# Revit family: Toilet_Universal-Wall_Hung-Sloan-ST-2469_Series
name_source: partatom
category: Plumbing Fixtures
revit_build: Autodesk Revit 2014 (Build: 20130308_1515(x64)
units: mm (PartAtom-declared; Revit-internal decimal feet)

## types (2) — shared parameters
ADA Compliant = Yes
Assembly Code = D2010110
CW Connection = Yes
CWFU = 1.5
Default Elevation = 16"
Fixture Color = White
Flush Volume = 1.1 to 1.6gpf/4.2 to 6.0 Lpf
HW Connection = No
Height = 13 1/4"
High Efficiency = Yes
IAPMO Compliance = cUPC
Inlet Spud Size = 1 1/2" I.P.S. Rear Spud Inlet
Length = 26 3/4"
Manufacturer = Sloan
Material = Vitreous China-Sloan-White
Mounting = Wall Hung
Price = Prices may vary. Please consult Sloan Rep for most up-to-date price list.
Product Documentation Link = https://specifications.sloan.com
Product Page URL = https://www.sloan.com
Spud Location = Rear Spud
URL = http://www.sloan.com
Vent Connection = No
WFU = 5
Waste Connection = Yes
Waste Connection Diameter = 2 1/8"
Width = 15"
zero-valued in all types: HWFU

## per-type parameters (varying)
| type | Description | Order Code |
| ST-2469-STG | Complete vitreous china water closet with SloanTec hydrophobic antimicrobial glaze. | 2172469 |
| ST-2469 | Complete vitreous china water closet. | 2102469 |

note: column(s) folded — value = type name in every type: Model

## geometry (parser evidence)
native form markers: Sweep x1
no freeform markers — native parametric forms only
